# Revit family: BE_84580_de_DE
name_source: partatom
category: Leuchten
units: mm (PartAtom-declared; Revit-internal decimal feet)

## family parameters
Basisbauteil = Fläche
Beim Laden mit Abzugskörper schneiden = Ja
Bemaßung runder Anschluss = Durchmesser verwenden
Gemeinsam genutzt = Nein
Lichtquelle = Nein
Raumberechnungspunkt = Ja
Teiletyp = Normal

## types (1)
- BEGA_84580_Grafit_K3
    AC/DC = AC/DC
    Aktualisierung = 2022-05-19T04:00:07
    Befestigungsabstand = 230 mm
    Befestigungsbohrung = Ø 5,3 mm
    Beschreibung = Scheinwerfer
    Beschreibung_Sonderanfertigung = Hier können Sie Informationen zur Sonderanfertigung eintragen.
    Bestellnummer = 84580K3
    CE_Konformität = ja
    Energieeffizienzklasse = LED A++ - A
    Farbtemperatur = 3000 K
    Farbwiedergabeindex = CRI > 90
    Frequenz = 0/50-60 Hz
    Gewicht = 1.5 kg
    Hersteller = BEGA
    LED_Modulbezeichnung = 2x LED-1217/930
    Lampe = LED 10.8 W
    Lampenlichtstrom = 1330 lm
    Lastklassifizierung = Beleuchtung
    Lebensdauerkriterien = L70B50 @ 25 °C =  h
    Leuchtenlichtstrom = 964 lm
    Logo = BEGA_Logo.png
    Material_06 = BEGA_Oberfläche_Edelstahl_gebürstet
    Material_09 = BEGA_Glas_klar
    Material_15 = BEGA_Leuchtmedium_matt
    Material_17 = BEGA_Reflektor
    Material_18 = BEGA_Gummi_schwarz
    Modell = 84580K3
    Produktdatenblatt = https://cdn.bega.com
    Scheinlast = 0 VA
    Schutzart = IP 65
    Schutzklasse = I
    Sonderanfertigung = Nein
    Spannung = 240 V
    URL = https://www.bega.com
    Umgebungstemperatur = 25 °C
    Vorgabe-Ansicht = 0 mm  [stored 0 ft]

note: [stored X ft] marks values corroborated as IEEE doubles in the binary element streams (Revit-internal decimal feet)

## geometry (parser evidence)
native form markers: Blend x2, Sweep x41
no freeform markers — native parametric forms only
